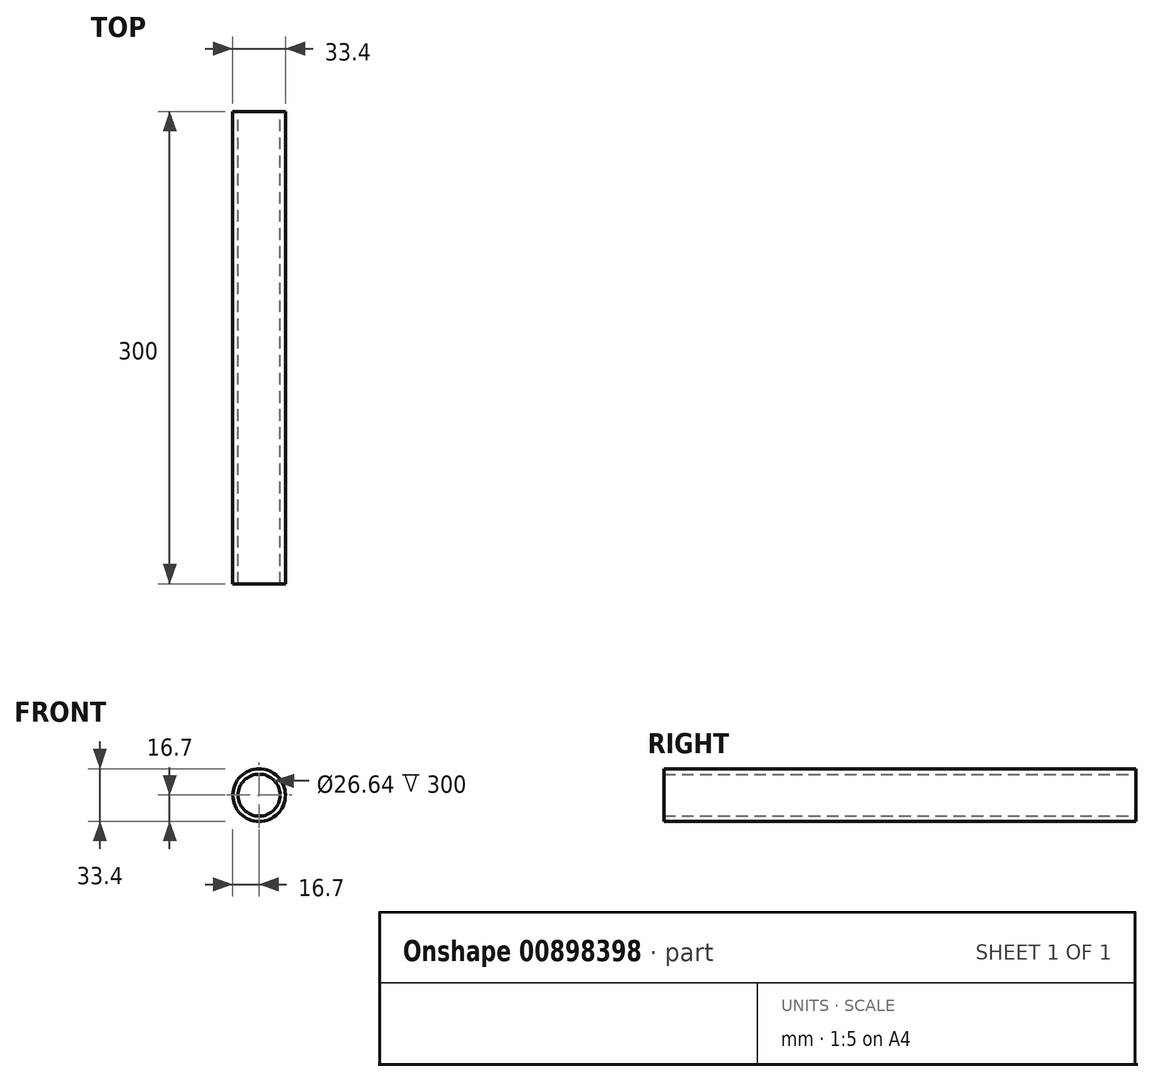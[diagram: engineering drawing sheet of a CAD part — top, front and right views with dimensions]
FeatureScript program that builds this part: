
annotation { "Feature Type Name" : "Feature", "Feature Type Description" : "" }
export const myFeature = defineFeature(function(context is Context, id is Id, definition is map)
    precondition{}
    {
        {
            var Q0;
            Q0=qCreatedBy(makeId("Front.planeOp"),FACE);
            var sketch = newSketch(context, id + "F0", { "sketchPlane" : qUnion([Q0])});
            skCircle(sketch, "E0", {"center": v(0, 0) * mm, "radius": 16.7 * mm});
            skCircle(sketch, "E1", {"center": v(0, 0) * mm, "radius": 13.32 * mm});
            skSolve(sketch);
        }
        {
            var Q0;
            Q0=makeQuery(id+"F0.imprint","IMPRINT",FACE,{"disambiguationData":[TD([[makeQuery(id+"F0.imprint","IMPRINT",EDGE,{"derivedFrom":sQuery(id+"F0.wireOp",EDGE,"E0")}),1.0]])]});
            extrude(context, id + "F1", {"entities" : qUnion([Q0]), "depth" : 300 * mm, "offsetDistance" : 25.4 * mm});
        }
    });
